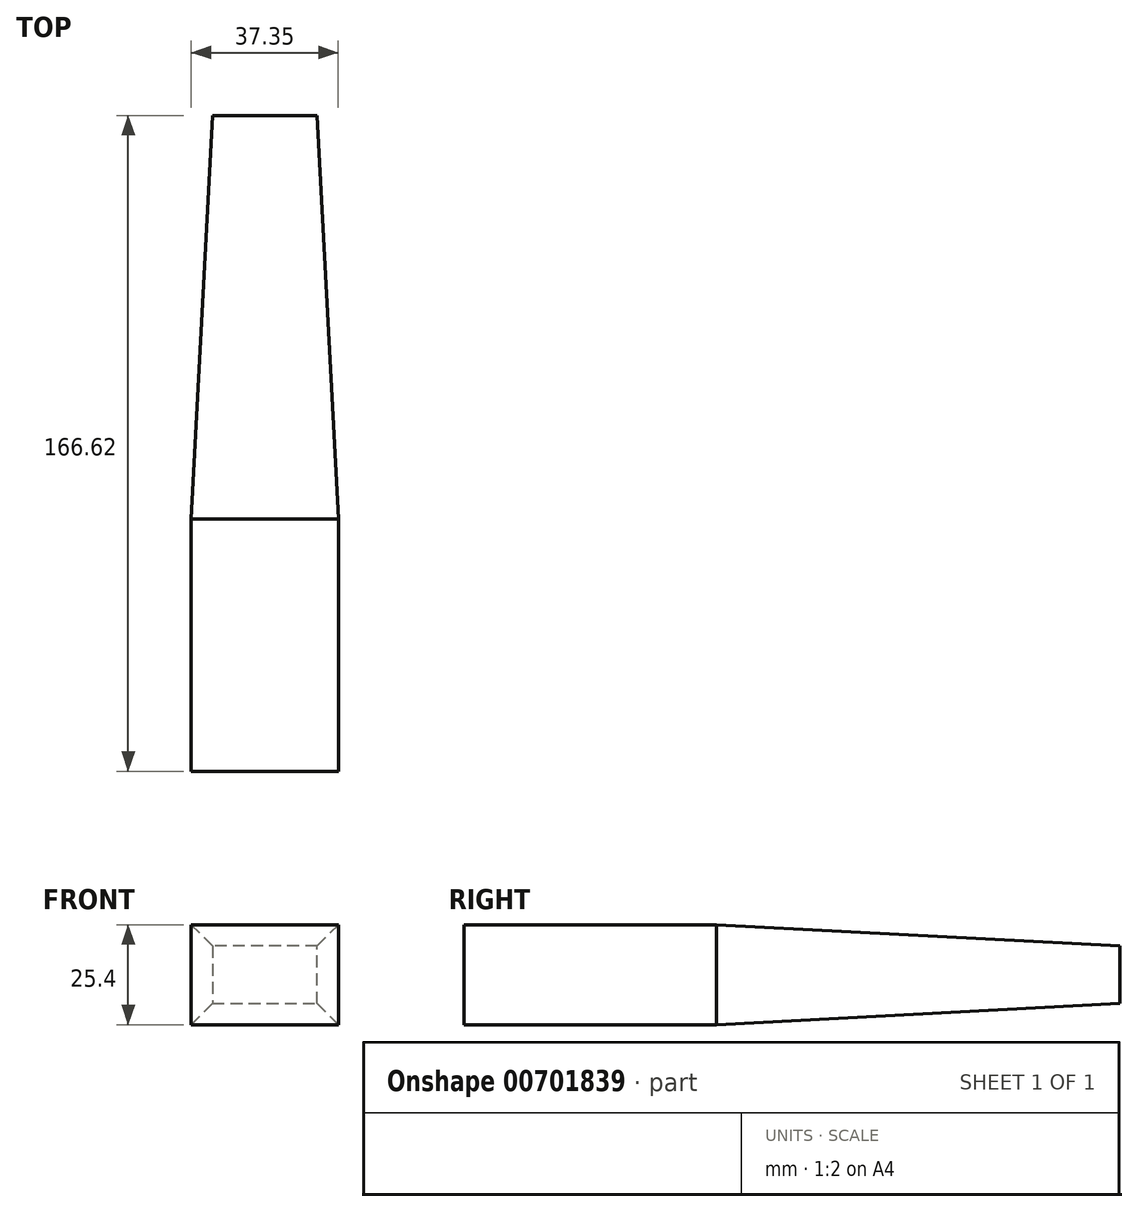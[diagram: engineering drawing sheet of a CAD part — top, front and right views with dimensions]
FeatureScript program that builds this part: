
annotation { "Feature Type Name" : "Feature", "Feature Type Description" : "" }
export const myFeature = defineFeature(function(context is Context, id is Id, definition is map)
    precondition{}
    {
        {
            var Q0;
            Q0=qCreatedBy(makeId("Top.planeOp"),FACE);
            var sketch = newSketch(context, id + "F0", { "sketchPlane" : qUnion([Q0])});
            skLineSegment(sketch, "E0.bottom", {"start": v(-36.4, 21.84) * mm, "end": v(38.31, 21.84) * mm});
            skLineSegment(sketch, "E0.top", {"start": v(-36.4, -42.28) * mm, "end": v(38.31, -42.28) * mm});
            skLineSegment(sketch, "E0.left", {"start": v(-36.4, 21.84) * mm, "end": v(-36.4, -42.28) * mm});
            skLineSegment(sketch, "E0.right", {"start": v(38.31, 21.84) * mm, "end": v(38.31, -42.28) * mm});
            skLineSegment(sketch, "E1", {"start": v(0.96, 36.85) * mm, "end": v(0.96, -42.28) * mm});
            skPoint(sketch, "E1.startSnap0", {"position": v(0.96, 21.84) * mm});
            skSolve(sketch);
        }
        {
            var Q0;
            {var subQ0=sQuery(id+"F0.wireOp",EDGE,"E0.right");Q0=makeQuery(id+"F0.imprint","IMPRINT",FACE,{"disambiguationData":[TD([[makeQuery(id+"F0.imprint","IMPRINT",EDGE,{"derivedFrom":subQ0}),-1.0]])]});}
            extrude(context, id + "F1", {"entities" : qUnion([Q0]), "depth" : 25.4 * mm, "offsetDistance" : 25.4 * mm});
        }
        {
            var Q0;
            Q0=makeQuery(id+"F1.opExtrude","SWEPT_FACE",FACE,{"disambiguationData":[OSD([sQuery(id+"F0.wireOp",EDGE,"E0.bottom")])]});
            extrude(context, id + "F2", {"entities" : qUnion([Q0]), "operationType" : NewBodyOperationType.ADD, "depth" : 102.5 * mm, "offsetDistance" : 25.4 * mm, "hasDraft" : true, "draftAngle" : 3 * degree, "draftPullDirection" : true});
        }
    });
